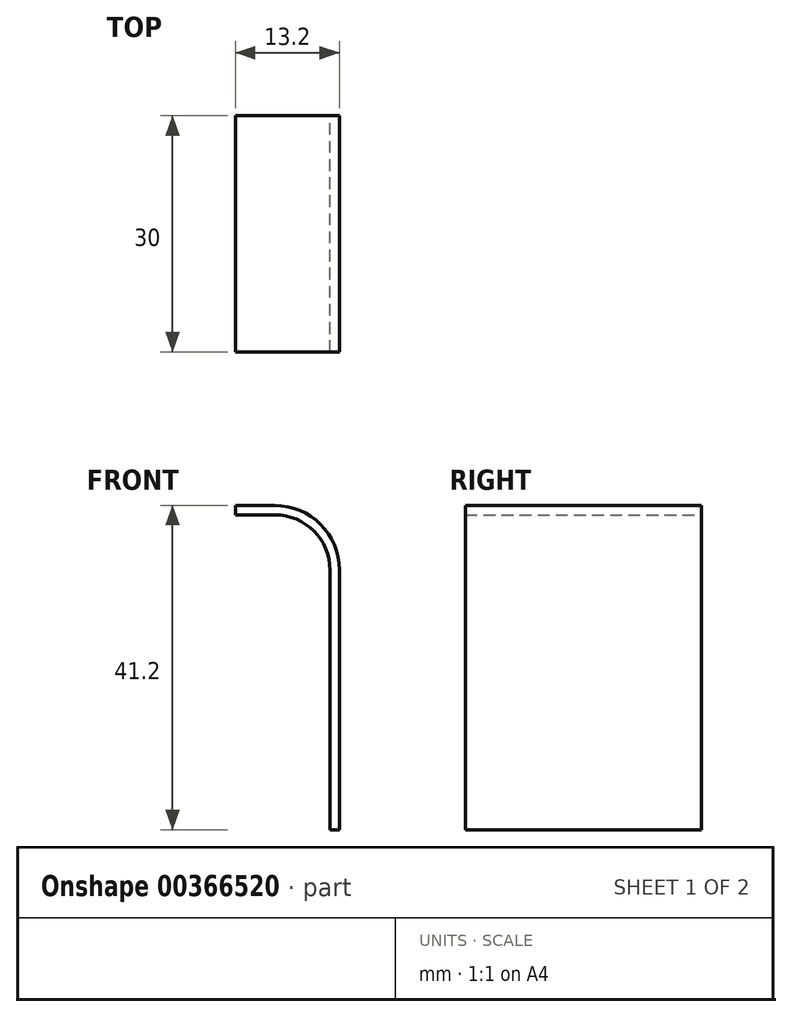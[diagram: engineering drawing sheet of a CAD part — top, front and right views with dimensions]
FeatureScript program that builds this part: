
annotation { "Feature Type Name" : "Feature", "Feature Type Description" : "" }
export const myFeature = defineFeature(function(context is Context, id is Id, definition is map)
    precondition{}
    {
        {
            var Q0;
            Q0=qCreatedBy(makeId("Front.planeOp"),FACE);
            var sketch = newSketch(context, id + "F0", { "sketchPlane" : qUnion([Q0])});
            skLineSegment(sketch, "E0.bottom", {"start": v(0, 0) * mm, "end": v(1.2, 0) * mm});
            skLineSegment(sketch, "E0.top", {"start": v(0, 33) * mm, "end": v(1.2, 33) * mm});
            skLineSegment(sketch, "E0.left", {"start": v(0, 0) * mm, "end": v(0, 33) * mm});
            skLineSegment(sketch, "E0.right", {"start": v(1.2, 0) * mm, "end": v(1.2, 33) * mm});
            skArc(sketch, "E1", {"start": v(0, 33) * mm, "mid": v(-2.05, 37.95) * mm, "end": v(-7, 40) * mm});
            skLineSegment(sketch, "E2", {"start": v(-7, 40) * mm, "end": v(-12, 40) * mm});
            skArc(sketch, "E3", {"start": v(1.2, 33) * mm, "mid": v(-1.2, 38.8) * mm, "end": v(-7, 41.2) * mm});
            skLineSegment(sketch, "E4", {"start": v(-7, 41.2) * mm, "end": v(-12, 41.2) * mm});
            skLineSegment(sketch, "E5", {"start": v(-12, 41.2) * mm, "end": v(-12, 40) * mm});
            skSolve(sketch);
        }
        {
            var Q0;
            Q0 = qSketchRegion(id + "F0", true);
            extrude(context, id + "F1", {"entities" : qUnion([Q0]), "depth" : 30 * mm});
        }
    });
